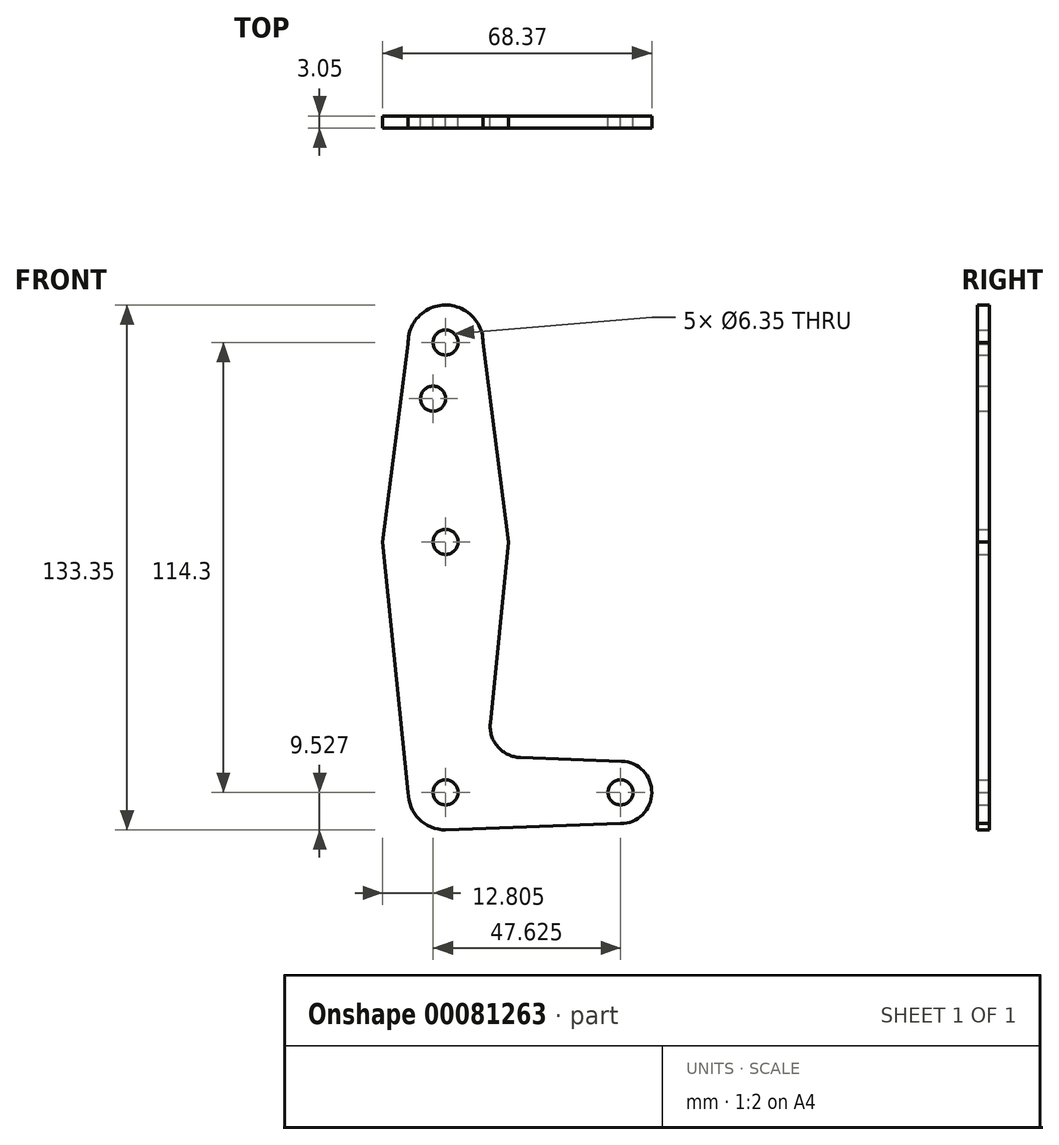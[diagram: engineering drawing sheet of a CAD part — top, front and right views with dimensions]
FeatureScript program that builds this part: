
annotation { "Feature Type Name" : "Feature", "Feature Type Description" : "" }
export const myFeature = defineFeature(function(context is Context, id is Id, definition is map)
    precondition{}
    {
        {
            var Q0;
            Q0=qCreatedBy(makeId("Front.planeOp"),FACE);
            var sketch = newSketch(context, id + "F0", { "sketchPlane" : qUnion([Q0])});
            skLineSegment(sketch, "E0", {"start": v(0, -25.48) * mm, "end": v(0, -63.66) * mm, "construction": true});
            skCircle(sketch, "E1", {"center": v(0, -63.66) * mm, "radius": 9.53 * mm});
            skCircle(sketch, "E2", {"center": v(0, 50.64) * mm, "radius": 9.53 * mm});
            skCircle(sketch, "E3", {"center": v(0, -0.16) * mm, "radius": 15.88 * mm});
            skLineSegment(sketch, "E4", {"start": v(0, -63.66) * mm, "end": v(0, -0.16) * mm, "construction": true});
            skLineSegment(sketch, "E5", {"start": v(0, 50.64) * mm, "end": v(0, -0.16) * mm, "construction": true});
            skCircle(sketch, "E6", {"center": v(44.45, -63.66) * mm, "radius": 7.94 * mm});
            skLineSegment(sketch, "E7", {"start": v(0, -63.66) * mm, "end": v(44.45, -63.66) * mm, "construction": true});
            skLineSegment(sketch, "E8", {"start": v(-9.52, 50.29) * mm, "end": v(-15.98, 0) * mm});
            skLineSegment(sketch, "E9", {"start": v(9.52, 50.64) * mm, "end": v(15.98, 0) * mm});
            skLineSegment(sketch, "E10", {"start": v(-15.98, 0) * mm, "end": v(-9.52, -63.66) * mm});
            skLineSegment(sketch, "E11", {"start": v(15.98, 0) * mm, "end": v(11.34, -46.07) * mm});
            skLineSegment(sketch, "E12", {"start": v(18.97, -54.81) * mm, "end": v(44.73, -55.73) * mm});
            skLineSegment(sketch, "E13", {"start": v(0, -73.19) * mm, "end": v(44.45, -71.6) * mm});
            skCircle(sketch, "E14", {"center": v(-3.18, 36.36) * mm, "radius": 3.18 * mm});
            skLineSegment(sketch, "E15", {"start": v(0, 0) * mm, "end": v(0, 25.24) * mm});
            skArc(sketch, "E16.filletArc", {"start": v(11.34, -46.07) * mm, "mid": v(13.26, -52.1) * mm, "end": v(18.97, -54.81) * mm});
            skCircle(sketch, "E17", {"center": v(44.45, -63.66) * mm, "radius": 3.18 * mm});
            skCircle(sketch, "E18", {"center": v(0, 0) * mm, "radius": 3.18 * mm});
            skCircle(sketch, "E19", {"center": v(0, 50.64) * mm, "radius": 3.18 * mm});
            skCircle(sketch, "E20", {"center": v(0, -63.66) * mm, "radius": 3.18 * mm});
            skSolve(sketch);
        }
        {
            var Q0;
            Q0=makeQuery(id+"F0.imprint","IMPRINT",FACE,{"disambiguationData":[TD([[makeQuery(id+"F0.imprint","IMPRINT",EDGE,{"derivedFrom":sQuery(id+"F0.wireOp",EDGE,"E19")}),-1.0]])]});
            var Q1;
            Q1=makeQuery(id+"F0.imprint","IMPRINT",FACE,{"disambiguationData":[TD([[makeQuery(id+"F0.imprint","IMPRINT",EDGE,{"derivedFrom":sQuery(id+"F0.wireOp",EDGE,"E14")}),-1.0]])]});
            var Q2;
            Q2=makeQuery(id+"F0.imprint","IMPRINT",FACE,{"disambiguationData":[TD([[makeQuery(id+"F0.imprint","IMPRINT",EDGE,{"derivedFrom":sQuery(id+"F0.wireOp",EDGE,"E18")}),-1.0]])]});
            var Q3;
            {var subQ0=sQuery(id+"F0.wireOp",EDGE,"E10");Q3=makeQuery(id+"F0.imprint","IMPRINT",FACE,{"disambiguationData":[TD([[makeQuery(id+"F0.imprint","IMPRINT",EDGE,{"derivedFrom":subQ0}),1.0]])]});}
            var Q4;
            Q4=makeQuery(id+"F0.imprint","IMPRINT",FACE,{"disambiguationData":[TD([[makeQuery(id+"F0.imprint","IMPRINT",EDGE,{"derivedFrom":sQuery(id+"F0.wireOp",EDGE,"E20")}),-1.0]])]});
            var Q5;
            Q5=makeQuery(id+"F0.imprint","IMPRINT",FACE,{"disambiguationData":[TD([[makeQuery(id+"F0.imprint","IMPRINT",EDGE,{"derivedFrom":sQuery(id+"F0.wireOp",EDGE,"E17")}),-1.0]])]});
            extrude(context, id + "F1", {"entities" : qUnion([Q0, Q1, Q2, Q3, Q4, Q5]), "depth" : 3.05 * mm});
        }
    });
